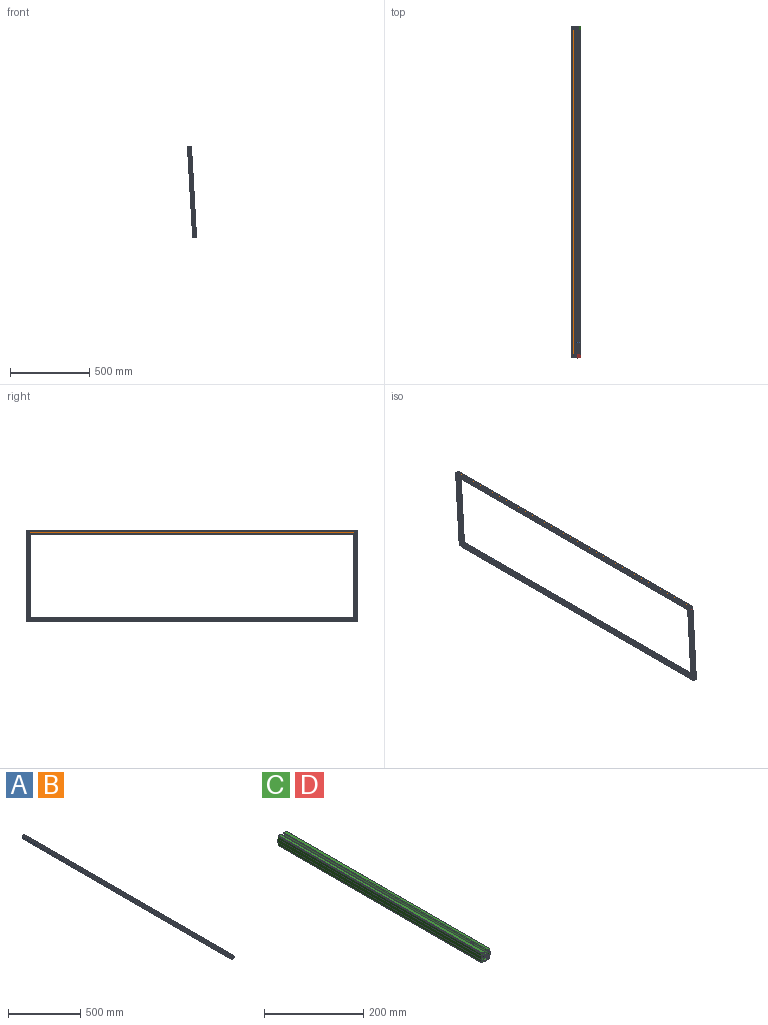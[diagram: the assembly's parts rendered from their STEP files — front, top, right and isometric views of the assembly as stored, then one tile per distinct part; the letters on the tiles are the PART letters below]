
ASSEMBLY  parts=4 mates=3
PART A: 65 faces, bbox 25x2044.7x25 mm
  f0: plane 2044.7x3.11mm, normal (0,0,-1), area 6359mm2, adj f1,f62,f63,f64
  f1: cylinder r=3.17mm len=2044.7mm, axis (0,1,0), area 5086.7mm2, adj f0,f2,f63,f64
  f2: plane 2044.7x3.34mm, normal (-0.71,0,-0.71), area 9646.1mm2, adj f1,f3,f63,f64
  f3: cylinder r=1.01mm len=2044.7mm, axis (0,1,0), area 4866.8mm2, adj f2,f4,f63,f64
  f4: plane 2044.7x2.1mm, normal (0,0,1), area 4293.9mm2, adj f3,f5,f63,f64
  f5: plane 2044.7x8.64mm, normal (0,0,1), area 17666.2mm2, adj f4,f6,f63,f64
  f6: plane 2044.7x2.1mm, normal (0,0,1), area 4293.9mm2, adj f5,f7,f63,f64
  f7: cylinder r=1.01mm len=2044.7mm, axis (0,1,0), area 4866.8mm2, adj f6,f8,f63,f64
  f8: plane 2044.7x3.34mm, normal (0.71,0,-0.71), area 9646.1mm2, adj f7,f62,f63,f64
  f9: plane 2044.7x1.56mm, normal (1,0,0), area 3179.6mm2, adj f10,f59,f63,f64
  f10: plane 2044.7x1.56mm, normal (1,0,0), area 3179.6mm2, adj f9,f11,f63,f64
  f11: cylinder r=3.17mm len=2044.7mm, axis (0,1,0), area 5086.7mm2, adj f10,f12,f63,f64
  f12: plane 2044.7x3.34mm, normal (0.71,0,-0.71), area 9646.1mm2, adj f11,f13,f63,f64
  f13: cylinder r=1.01mm len=2044.7mm, axis (0,1,0), area 4866.8mm2, adj f12,f14,f63,f64
  f14: plane 2044.7x2.1mm, normal (-1,0,0), area 4293.9mm2, adj f13,f15,f63,f64
  f15: plane 2044.7x8.64mm, normal (-1,0,0), area 17666.5mm2, adj f14,f16,f63,f64
  f16: plane 2044.7x2.1mm, normal (-1,0,0), area 4293.9mm2, adj f15,f17,f63,f64
  f17: cylinder r=1.01mm len=2044.7mm, axis (0,1,0), area 4866.8mm2, adj f16,f18,f63,f64
  f18: plane 2044.7x3.34mm, normal (0.71,0,0.71), area 9646.1mm2, adj f17,f59,f63,f64
  f19: cylinder r=1.01mm len=2044.7mm, axis (0,1,0), area 4866.8mm2, adj f20,f60,f63,f64
  f20: plane 2044.7x2.1mm, normal (0,0,-1), area 4293.9mm2, adj f19,f21,f63,f64
  f21: cylinder r=1.07mm len=2044.7mm, axis (0,1,0), area 6871.6mm2, adj f20,f22,f63,f64
  f22: plane 2044.7x6.22mm, normal (0,0,1), area 12712mm2, adj f21,f23,f63,f64
  f23: cylinder r=1.96mm len=2044.7mm, axis (0,1,0), area 3149.2mm2, adj f22,f24,f63,f64
  f24: cylinder r=1.96mm len=2044.7mm, axis (0,1,0), area 3149.2mm2, adj f23,f25,f63,f64
  f25: plane 2044.7x6.22mm, normal (-1,0,0), area 12712mm2, adj f24,f26,f63,f64
  f26: plane 2044.7x8.64mm, normal (-1,0,0), area 17666.5mm2, adj f25,f27,f63,f64
  f27: plane 2044.7x6.22mm, normal (-1,0,0), area 12712mm2, adj f26,f28,f63,f64
  f28: cylinder r=1.96mm len=2044.7mm, axis (0,1,0), area 3149.2mm2, adj f27,f29,f63,f64
  f29: cylinder r=1.96mm len=2044.7mm, axis (0,1,0), area 3149.2mm2, adj f28,f30,f63,f64
  f30: plane 2044.7x6.22mm, normal (0,0,-1), area 12712mm2, adj f29,f31,f63,f64
  f31: plane 2044.7x8.64mm, normal (0,0,-1), area 17666.2mm2, adj f30,f32,f63,f64
  f32: plane 2044.7x6.22mm, normal (0,0,-1), area 12712mm2, adj f31,f33,f63,f64
  f33: cylinder r=1.96mm len=2044.7mm, axis (0,1,0), area 3149.2mm2, adj f32,f34,f63,f64
  f34: cylinder r=1.96mm len=2044.7mm, axis (0,1,0), area 3149.2mm2, adj f33,f35,f63,f64
  f35: plane 2044.7x6.22mm, normal (1,0,0), area 12712mm2, adj f34,f36,f63,f64
  f36: plane 2044.7x8.64mm, normal (1,0,0), area 17666.5mm2, adj f35,f37,f63,f64
  f37: plane 2044.7x6.22mm, normal (1,0,0), area 12712mm2, adj f36,f38,f63,f64
  f38: cylinder r=1.96mm len=2044.7mm, axis (0,1,0), area 3149.2mm2, adj f37,f39,f63,f64
  f39: cylinder r=1.96mm len=2044.7mm, axis (0,1,0), area 3149.2mm2, adj f38,f40,f63,f64
  f40: plane 2044.7x6.22mm, normal (0,0,1), area 12712mm2, adj f39,f41,f63,f64
  f41: cylinder r=1.07mm len=2044.7mm, axis (0,1,0), area 6868.6mm2, adj f40,f42,f63,f64
  f42: plane 2044.7x2.1mm, normal (0,0,-1), area 4293.9mm2, adj f41,f43,f63,f64
  f43: cylinder r=1.01mm len=2044.7mm, axis (0,1,0), area 4866.8mm2, adj f42,f44,f63,f64
  f44: plane 2044.7x3.34mm, normal (-0.71,0,0.71), area 9646.1mm2, adj f43,f45,f63,f64
  f45: cylinder r=3.17mm len=2044.7mm, axis (0,1,0), area 5086.7mm2, adj f44,f46,f63,f64
  f46: plane 2044.7x3.11mm, normal (0,0,1), area 6359mm2, adj f45,f47,f63,f64
  f47: cylinder r=3.17mm len=2044.7mm, axis (0,1,0), area 5086.7mm2, adj f46,f60,f63,f64
  f48: plane 2044.7x1.56mm, normal (-1,0,0), area 3179.6mm2, adj f49,f61,f63,f64
  f49: plane 2044.7x1.56mm, normal (-1,0,0), area 3179.6mm2, adj f48,f50,f63,f64
  f50: cylinder r=3.17mm len=2044.7mm, axis (0,1,0), area 5086.7mm2, adj f49,f51,f63,f64
  f51: plane 2044.7x3.34mm, normal (-0.71,0,0.71), area 9646.1mm2, adj f50,f52,f63,f64
  f52: cylinder r=1.01mm len=2044.7mm, axis (0,1,0), area 4866.8mm2, adj f51,f53,f63,f64
  f53: plane 2044.7x2.1mm, normal (1,0,0), area 4293.9mm2, adj f52,f54,f63,f64
  f54: plane 2044.7x8.64mm, normal (1,0,0), area 17666.5mm2, adj f53,f55,f63,f64
  f55: plane 2044.7x2.1mm, normal (1,0,0), area 4293.9mm2, adj f54,f56,f63,f64
  f56: cylinder r=1.01mm len=2044.7mm, axis (0,1,0), area 4866.8mm2, adj f55,f57,f63,f64
  f57: plane 2044.7x3.34mm, normal (-0.71,0,-0.71), area 9646.1mm2, adj f56,f61,f63,f64
  f58: cylinder r=2.5mm len=2044.7mm, axis (0,1,0), area 32118.1mm2, adj f63,f64
  f59: cylinder r=3.17mm len=2044.7mm, axis (0,1,0), area 5086.7mm2, adj f9,f18,f63,f64
  f60: plane 2044.7x3.34mm, normal (0.71,0,0.71), area 9646.1mm2, adj f19,f47,f63,f64
  f61: cylinder r=3.17mm len=2044.7mm, axis (0,1,0), area 5086.7mm2, adj f48,f57,f63,f64
  f62: cylinder r=3.17mm len=2044.7mm, axis (0,1,0), area 5086.7mm2, adj f0,f8,f63,f64
  f63: plane 25x25mm, normal (0,-1,0), area 318mm2, adj f0,f1,f2,f3,f4,f5,f6,f7
  f64: plane 25x25mm, normal (0,1,0), area 318mm2, adj f0,f1,f2,f3,f4,f5,f6,f7
PART B: same geometry as A
PART C: 92 faces, bbox 25x577.9x25 mm
  f0: cylinder r=3.17mm len=38.59mm, axis (0,1,0), area 94.8mm2, adj f1,f2,f80,f91
  f1: plane 37.61x3.13mm, normal (0,0,-1), area 116.6mm2, adj f0,f4,f80,f91
  f2: plane 577.86x3.35mm, normal (-0.71,0,-0.71), area 2690.9mm2, adj f0,f23,f24,f80,f81,f90,f91
  f3: plane 577.86x3.35mm, normal (0.71,0,-0.71), area 2690.9mm2, adj f4,f22,f28,f80,f81,f90,f91
  f4: cylinder r=3.17mm len=38.59mm, axis (0,1,0), area 94.8mm2, adj f1,f3,f80,f91
  f5: cylinder r=6.6mm len=13.21mm, axis (0,0,-1), area 125.8mm2, adj f10,f11,f12,f15,f16,f17,f18,f19
  f6: plane 526.56x3.12mm, normal (0,0,-1), area 1637.2mm2, adj f22,f23,f81,f90
  f7: plane 531.44x2.11mm, normal (0,0,1), area 1112mm2, adj f8,f24,f81,f90
  f8: plane 528.27x8.65mm, normal (0,0,1), area 4554.9mm2, adj f7,f9,f81,f90
  f9: plane 531.44x2.11mm, normal (0,0,1), area 1112mm2, adj f8,f28,f81,f90
  f10: plane 39.5x1.56mm, normal (1,0,0), area 61.4mm2, adj f5,f30,f77,f80
  f11: plane 528.45x1.56mm, normal (1,0,0), area 821.8mm2, adj f5,f29,f31,f81
  f12: cylinder r=3.17mm len=40.51mm, axis (0,1,0), area 99.5mm2, adj f5,f30,f32,f80
  f13: plane 577.85x13.26mm, normal (0,0,-1), area 4975mm2, adj f14,f50,f80,f81,f85
  f14: plane 577.85x6.25mm, normal (0,0,-1), area 3576.7mm2, adj f13,f51,f80,f81
  f15: plane 526.98x3.11mm, normal (0,0,1), area 1638.5mm2, adj f5,f63,f65,f81
  f16: plane 528.45x1.56mm, normal (-1,0,0), area 821.8mm2, adj f5,f21,f67,f81
  f17: plane 39.5x1.56mm, normal (-1,0,0), area 61.4mm2, adj f5,f18,f66,f80
  f18: cylinder r=3.17mm len=39.79mm, axis (0,1,0), area 98.1mm2, adj f5,f17,f69,f80,f84,f86,f87
  f19: cylinder r=2.5mm len=37.85mm, axis (0,1,0), area 594.5mm2, adj f5,f80
  f20: cylinder r=3.17mm len=528.74mm, axis (0,1,0), area 1314.6mm2, adj f5,f29,f38,f81,f87,f89
  f21: cylinder r=3.17mm len=529.46mm, axis (0,1,0), area 1315.9mm2, adj f5,f16,f75,f81
  f22: cylinder r=3.17mm len=527.54mm, axis (0,1,0), area 1311.1mm2, adj f3,f6,f81,f90
  f23: cylinder r=3.17mm len=527.54mm, axis (0,1,0), area 1311.1mm2, adj f2,f6,f81,f90
  f24: cylinder r=1.01mm len=577.85mm, axis (0,1,0), area 1374.6mm2, adj f2,f7,f25,f80,f81,f90
  f25: plane 42.49x2.11mm, normal (0,0,1), area 85.2mm2, adj f24,f26,f80,f90
  f26: plane 39.33x8.66mm, normal (0,0,1), area 330.3mm2, adj f25,f27,f80,f90,f91
  f27: plane 42.49x2.11mm, normal (0,0,1), area 85.2mm2, adj f26,f28,f80,f90
  f28: cylinder r=1.01mm len=577.85mm, axis (0,1,0), area 1374.6mm2, adj f3,f9,f27,f80,f81,f90
  f29: plane 528.45x1.56mm, normal (1,0,0), area 821.8mm2, adj f5,f11,f20,f81
  f30: plane 39.5x1.56mm, normal (1,0,0), area 61.4mm2, adj f5,f10,f12,f80
  f31: cylinder r=3.17mm len=529.46mm, axis (0,1,0), area 1315.9mm2, adj f5,f11,f32,f81
  f32: plane 577.85x3.34mm, normal (0.71,0,-0.71), area 2716.2mm2, adj f5,f12,f31,f33,f80,f81
  f33: cylinder r=1.01mm len=577.85mm, axis (0,1,0), area 1375.4mm2, adj f32,f34,f80,f81
  f34: plane 577.85x2.1mm, normal (-1,0,0), area 1213.5mm2, adj f33,f35,f80,f81
  f35: plane 577.85x8.64mm, normal (-1,0,0), area 4992.7mm2, adj f34,f36,f80,f81
  f36: plane 577.85x2.1mm, normal (-1,0,0), area 1213.5mm2, adj f35,f37,f80,f81
  f37: cylinder r=1.01mm len=577.85mm, axis (0,1,0), area 1375.4mm2, adj f36,f38,f80,f81
  f38: plane 577.85x3.34mm, normal (0.71,0,0.71), area 2711mm2, adj f20,f37,f77,f80,f81,f89
  f39: cylinder r=1.01mm len=577.85mm, axis (0,1,0), area 1375.4mm2, adj f40,f78,f80,f81
  f40: plane 577.85x2.1mm, normal (0,0,-1), area 1213.5mm2, adj f39,f41,f80,f81
  f41: cylinder r=1.07mm len=577.85mm, axis (0,1,0), area 1942mm2, adj f40,f42,f80,f81
  f42: plane 577.85x6.22mm, normal (0,0,1), area 3592.5mm2, adj f41,f43,f80,f81
  f43: cylinder r=1.96mm len=577.85mm, axis (0,1,0), area 890mm2, adj f42,f44,f80,f81
  f44: cylinder r=1.96mm len=577.85mm, axis (0,1,0), area 890mm2, adj f43,f45,f80,f81
  f45: plane 577.85x6.22mm, normal (-1,0,0), area 3592.5mm2, adj f44,f46,f80,f81
  f46: plane 577.85x8.64mm, normal (-1,0,0), area 4992.7mm2, adj f45,f47,f80,f81
  f47: plane 577.85x6.22mm, normal (-1,0,0), area 3592.5mm2, adj f46,f48,f80,f81
  f48: cylinder r=1.96mm len=577.85mm, axis (0,1,0), area 890mm2, adj f47,f49,f80,f81
  f49: cylinder r=1.96mm len=577.85mm, axis (0,1,0), area 890mm2, adj f48,f50,f80,f81
  f50: plane 577.85x6.25mm, normal (0,0,-1), area 3576.7mm2, adj f13,f49,f80,f81
  f51: cylinder r=1.96mm len=577.85mm, axis (0,1,0), area 890mm2, adj f14,f52,f80,f81
  f52: cylinder r=1.96mm len=577.85mm, axis (0,1,0), area 890mm2, adj f51,f53,f80,f81
  f53: plane 577.85x6.22mm, normal (1,0,0), area 3592.5mm2, adj f52,f54,f80,f81
  f54: plane 577.85x8.64mm, normal (1,0,0), area 4992.7mm2, adj f53,f55,f80,f81
  f55: plane 577.85x6.22mm, normal (1,0,0), area 3592.5mm2, adj f54,f56,f80,f81
  f56: cylinder r=1.96mm len=577.85mm, axis (0,1,0), area 890mm2, adj f55,f57,f80,f81
  f57: cylinder r=1.96mm len=577.85mm, axis (0,1,0), area 890mm2, adj f56,f58,f80,f81
  f58: plane 577.85x6.22mm, normal (0,0,1), area 3592.5mm2, adj f57,f59,f80,f81
  f59: cylinder r=1.07mm len=577.85mm, axis (0,1,0), area 1941.1mm2, adj f58,f60,f80,f81
  f60: plane 577.85x2.1mm, normal (0,0,-1), area 1213.5mm2, adj f59,f61,f80,f81
  f61: cylinder r=1.01mm len=577.85mm, axis (0,1,0), area 1375.4mm2, adj f60,f62,f80,f81
  f62: plane 577.85x3.34mm, normal (-0.71,0,0.71), area 2726.1mm2, adj f61,f63,f80,f81
  f63: cylinder r=3.17mm len=577.85mm, axis (0,1,0), area 1408.5mm2, adj f5,f15,f62,f64,f80,f81,f83
  f64: plane 38.03x3.11mm, normal (0,0,1), area 117.9mm2, adj f5,f63,f65,f80
  f65: cylinder r=3.17mm len=577.85mm, axis (0,1,0), area 1408.5mm2, adj f5,f15,f64,f78,f80,f81,f82
  f66: plane 39.5x1.56mm, normal (-1,0,0), area 61.4mm2, adj f5,f17,f79,f80
  f67: plane 528.45x1.56mm, normal (-1,0,0), area 821.8mm2, adj f5,f16,f68,f81
  f68: cylinder r=3.17mm len=528.74mm, axis (0,1,0), area 1314.6mm2, adj f5,f67,f69,f81,f84,f87
  f69: plane 577.85x3.34mm, normal (-0.71,0,0.71), area 2711mm2, adj f18,f68,f70,f80,f81,f84
  f70: cylinder r=1.01mm len=577.85mm, axis (0,1,0), area 1375.4mm2, adj f69,f71,f80,f81
  f71: plane 577.85x2.1mm, normal (1,0,0), area 1213.5mm2, adj f70,f72,f80,f81
  f72: plane 577.85x8.64mm, normal (1,0,0), area 4992.7mm2, adj f71,f73,f80,f81
  f73: plane 577.85x2.1mm, normal (1,0,0), area 1213.5mm2, adj f72,f74,f80,f81
  f74: cylinder r=1.01mm len=577.85mm, axis (0,1,0), area 1375.4mm2, adj f73,f75,f80,f81
  f75: plane 577.85x3.34mm, normal (-0.71,0,-0.71), area 2716.2mm2, adj f5,f21,f74,f79,f80,f81
  f76: cylinder r=2.5mm len=526.8mm, axis (0,1,0), area 8274.9mm2, adj f5,f81
  f77: cylinder r=3.17mm len=39.79mm, axis (0,1,0), area 98.1mm2, adj f5,f10,f38,f80,f87,f88,f89
  f78: plane 577.85x3.34mm, normal (0.71,0,0.71), area 2726.1mm2, adj f39,f65,f80,f81
  f79: cylinder r=3.17mm len=40.51mm, axis (0,1,0), area 99.5mm2, adj f5,f66,f75,f80
  f80: plane 25x25mm, normal (0,-1,0), area 318mm2, adj f0,f1,f2,f3,f4,f10,f12,f13
  f81: plane 25x25mm, normal (0,1,0), area 318mm2, adj f2,f3,f6,f7,f8,f9,f11,f13
  f82: plane 10.84x2.83mm, normal (0,0,-1), area 21.5mm2, adj f5,f65
  f83: plane 10.84x2.83mm, normal (0,0,-1), area 21.5mm2, adj f5,f63
  f84: bspline ~11.9x11.78mm, area 25.1mm2, adj f18,f68,f69,f86,f87
  f85: cone r=3.96mm half-angle=3deg, axis (0,0,-1), area 230.8mm2, adj f13,f87
  f86: bspline ~11.9x0.67mm, area 0mm2, adj f18,f84,f87
  f87: plane 14.25x13.21mm, normal (0,0,1), area 111.8mm2, adj f5,f18,f20,f68,f77,f84,f85,f86
  f88: bspline ~11.9x0.67mm, area 0mm2, adj f77,f87,f89
  f89: bspline ~12x11.9mm, area 25.1mm2, adj f20,f38,f77,f87,f88
  f90: bspline ~14.47x12.91mm, area 121.3mm2, adj f2,f3,f6,f7,f8,f9,f22,f23
  f91: bspline ~11.9x9.41mm, area 52.8mm2, adj f0,f1,f2,f3,f4,f26,f90
PART D: same geometry as C
PLACE A rot(axis=(0,-1,0),3.2deg) t=(58.1,0,26.87)mm
PLACE B rot(axis=(0,1,0),176.7deg) t=(-67.45,0,689.82)mm
PLACE C rot(axis=(1,-0.03,0.03),90deg) t=(14.37,24.58,648.86)mm
PLACE D rot(axis=(-1,-0.03,-0.03),90deg) t=(47.37,-2069.28,71.9)mm
MATE fastened D.f81 <-> A.f30  axis (0.06,0,-1) through (1.33,-2044.7,69.33)mm
MATE fastened C.f81 <-> B.f30  axis (-0.06,0,1) through (-10.62,0,647.43)mm
MATE fastened A.f32 <-> C.f80  axis (0.06,0,-1) through (22.37,0,70.52)mm
